# Revit family: bfs-15_240sug2_tug2_tua2_60Hz
name_source: partatom
category: 機械設備
units: mm (PartAtom-declared; Revit-internal decimal feet)

## family parameters
OmniClass タイトル = Centrifugal Fans
OmniClass 番号 = 23.75.35.17.27
パーツ タイプ = 割り込み
ロード時にボイドで切り取り = いいえ
丸型コネクタ寸法 = 直径を使用
作業面ベース = いいえ
共有 = いいえ
常に垂直 = はい
部屋計算ポイント = はい

## types (18) — shared parameters
Clearance Left = 450  [stored 1.47638 ft]
IfcExportAs = IfcFanType
IfcExportType = CENTRIFUGALFORWARDCURVED
MID静圧 = 0.0 Pa
MID風量 = 0.0 m³/h
OmniClassCode = 23-33 31 19 13 15
URL = https://www.mitsubishielectric.co.jp
Uniclass2015Code = Pr_65_67_29_12
Uniclass2015Title = Centrifugal fans
Uniclass2015Version = Systems v1.9
サービススペース = はい
ファンの種類 = 多翼形
仕様書バージョン = Version1.0
企業コード = 108420
分類コード = 50052502100020
参照している仕様書等のバージョン = 公共建築工事標準仕様書（機械設備工事編）平成31年度版
周波数 = 60 Hz
呼称 = 消音ボックス付送風機
実風量 = 0.0 m³/h
形名 = BFS-SUG : BFS-15SUG
本体マテリアル = 溶融亜鉛めっき鋼板
極 = 4
法定耐用年数 = 15
盤工事区分 = 電気工事
積算_科目 = 2 換気設備
製品リリース年月 = 2022年6月1日
製品出荷対象 = 国内
製造元 = 三菱電機株式会社
設置方法 = 天吊
説明 = ストレートシロッコファン天吊埋込タイプ（消音形）
負荷分類 = 3_ファン類
運転質量 = 0.00 kg
zero-valued in all types: Clearance Back, Clearance Bottom, Clearance Front, Clearance Right, Clearance Top

## per-type parameters (varying)
| type | Depth | Height | M | MAX静圧 | MAX風量 | MIN静圧 | MIN風量 | Width | ダクト径 | 価格 | 天吊金具ピッチ奥行 | 天吊金具ピッチ幅 | 極数 | 消費電力 | 番手 | 相 | 製品質量 | 質量 | 電動機出力 | 電圧 | 騒音レベル(dB(A)) | 騒音レベル(dB(A))_側面 | 騒音レベル(dB(A))_吐出 | 騒音レベル(dB(A))_吸込 |
| BFS-15SUG2 | 360  [stored 1.1811 ft] | 225  [stored 0.738189 ft] | 60  [stored 0.19685 ft] | 62.0 Pa | 150.0 m³/h | 25.0 Pa | 96.0 m³/h | 273  [stored 0.895669 ft] | 100 mm | 59900 $ | 325  [stored 1.06627 ft] | 349  [stored 1.14501 ft] | 2 | 24 W | #1 | 1 | 7.00 kg | 8.40 kg | 8 W | 100 V | 33 | 19 | 33 | 22 |
| BFS-30SUG2 | 428  [stored 1.4042 ft] | 225  [stored 0.738189 ft] | 70  [stored 0.229659 ft] | 39.0 Pa | 300.0 m³/h | 15.0 Pa | 182.0 m³/h | 273  [stored 0.895669 ft] | 150 mm | 83300 $ | 393  [stored 1.28937 ft] | 349  [stored 1.14501 ft] | 2 | 45 W | #1 | 1 | 7.50 kg | 9.00 kg | 16 W | 100 V | 40 | 19.5 | 40 | 26.5 |
| BFS-40SUG2 | 454  [stored 1.4895 ft] | 255  [stored 0.836614 ft] | 70  [stored 0.229659 ft] | 78.0 Pa | 400.0 m³/h | 37.0 Pa | 273.0 m³/h | 305  [stored 1.00066 ft] | 150 mm | 99500 $ | 419 | 381  [stored 1.25 ft] | 2 | 65 W | #1 1/4 | 1 | 9.50 kg | 11.40 kg | 25 W | 100 V | 44 | 20.5 | 44 | 27 |
| BFS-50SUG2 | 573  [stored 1.87992 ft] | 255  [stored 0.836614 ft] | 85  [stored 0.278871 ft] | 157.0 Pa | 500.0 m³/h | 81.0 Pa | 360.0 m³/h | 375  [stored 1.23031 ft] | 200 mm | 140000 $ | 538  [stored 1.76509 ft] | 451  [stored 1.47966 ft] | 2 | 88 W | #1 1/4 | 1 | 13.00 kg | 15.60 kg | 45 W | 100 V | 49 | 23 | 49 | 29.5 |
| BFS-65SUG2 | 638  [stored 2.09318 ft] | 305  [stored 1.00066 ft] | 85  [stored 0.278871 ft] | 157.0 Pa | 650.0 m³/h | 94.0 Pa | 501.0 m³/h | 423  [stored 1.3878 ft] | 200 mm | 148000 $ | 603 | 499  [stored 1.63714 ft] | 2 | 125 W | #1 1/4 | 1 | 16.00 kg | 19.20 kg | 65 W | 100 V | 51 | 24.5 | 51 | 29.5 |
| BFS-80SUG2 | 638  [stored 2.09318 ft] | 305  [stored 1.00066 ft] | 85  [stored 0.278871 ft] | 157.0 Pa | 800.0 m³/h | 84.0 Pa | 596.0 m³/h | 423  [stored 1.3878 ft] | 200 mm | 156000 $ | 603 | 499  [stored 1.63714 ft] | 2 | 159 W | #1 1/4 | 1 | 16.50 kg | 19.80 kg | 80 W | 100 V | 53 | 27 | 53 | 32 |
| BFS-90SUG2 | 638  [stored 2.09318 ft] | 305  [stored 1.00066 ft] | 85  [stored 0.278871 ft] | 206.0 Pa | 900.0 m³/h | 116.0 Pa | 676.0 m³/h | 443  [stored 1.45341 ft] | 200 mm | 164000 $ | 603 | 519 | 2 | 202 W | #1 1/2 | 1 | 18.50 kg | 22.20 kg | 110 W | 100 V | 55 | 29 | 55 | 34.5 |
| BFS-100SUG2 | 638  [stored 2.09318 ft] | 305  [stored 1.00066 ft] | 85  [stored 0.278871 ft] | 255.0 Pa | 1000.0 m³/h | 189.0 Pa | 861.0 m³/h | 443  [stored 1.45341 ft] | 200 mm | 176000 $ | 603 | 519 | 2 | 247 W | #1 1/2 | 1 | 19.00 kg | 22.80 kg | 160 W | 100 V | 58 | 31.5 | 58 | 37 |
| BFS-120SUG2 | 668 | 350  [stored 1.14829 ft] | 85  [stored 0.278871 ft] | 265.0 Pa | 1200.0 m³/h | 179.0 Pa | 989.0 m³/h | 455 | 250 mm | 194000 $ | 633  [stored 2.07677 ft] | 531  [stored 1.74213 ft] | 2 | 348 W | #1 1/2 | 1 | 22.00 kg | 26.40 kg | 200 W | 100 V | 58 | 32.5 | 58 | 41 |
| BFS-150SUG2 | 768 | 350  [stored 1.14829 ft] | 85  [stored 0.278871 ft] | 294.0 Pa | 1500.0 m³/h | 179.0 Pa | 1164.0 m³/h | 455 | 250 mm | 201000 $ | 733 | 531  [stored 1.74213 ft] | 2 | 484 W | #1 1/2 | 1 | 24.00 kg | 28.80 kg | 340 W | 100 V | 63 | 34 | 63 | 42.5 |
| BFS-80TUG2 | 638  [stored 2.09318 ft] | 305  [stored 1.00066 ft] | 85  [stored 0.278871 ft] | 157.0 Pa | 800.0 m³/h | 72.0 Pa | 542.0 m³/h | 423  [stored 1.3878 ft] | 200 mm | 156000 $ | 603 | 499  [stored 1.63714 ft] | 3 | 152 W | #1 1/4 | 3 | 18.00 kg | 21.60 kg | 80 W | 200 V | 53 | 26.5 | 53 | 32.5 |
| BFS-90TUG2 | 638  [stored 2.09318 ft] | 305  [stored 1.00066 ft] | 85  [stored 0.278871 ft] | 206.0 Pa | 900.0 m³/h | 95.0 Pa | 612.0 m³/h | 443  [stored 1.45341 ft] | 200 mm | 164000 $ | 603 | 519 | 3 | 187 W | #1 1/2 | 3 | 18.00 kg | 21.60 kg | 100 W | 200 V | 55 | 29 | 55 | 34.5 |
| BFS-100TUG2 | 638  [stored 2.09318 ft] | 305  [stored 1.00066 ft] | 85  [stored 0.278871 ft] | 255.0 Pa | 1000.0 m³/h | 124.0 Pa | 694.0 m³/h | 443  [stored 1.45341 ft] | 200 mm | 176000 $ | 603 | 519 | 3 | 230 W | #1 1/2 | 3 | 18.50 kg | 22.20 kg | 150 W | 200 V | 58 | 31 | 58 | 37 |
| BFS-120TUG2 | 668 | 350  [stored 1.14829 ft] | 85  [stored 0.278871 ft] | 265.0 Pa | 1200.0 m³/h | 119.0 Pa | 789.0 m³/h | 455 | 250 mm | 194000 $ | 633  [stored 2.07677 ft] | 531  [stored 1.74213 ft] | 3 | 319 W | #1 1/2 | 3 | 22.00 kg | 26.40 kg | 180 W | 200 V | 58 | 32.5 | 58 | 41 |
| BFS-150TUG2 | 768 | 350  [stored 1.14829 ft] | 85  [stored 0.278871 ft] | 294.0 Pa | 1500.0 m³/h | 142.0 Pa | 1046.0 m³/h | 455 | 250 mm | 201000 $ | 733 | 531  [stored 1.74213 ft] | 3 | 445 W | #1 1/2 | 3 | 24.00 kg | 28.80 kg | 280 W | 200 V | 63 | 34 | 63 | 42.5 |
| BFS-180TUG2 | 768 | 350  [stored 1.14829 ft] | 85  [stored 0.278871 ft] | 314.0 Pa | 1800.0 m³/h | 0.0 Pa | 0.0 m³/h | 505  [stored 1.65682 ft] | 250 mm | 236000 $ | 733 | 581  [stored 1.90617 ft] | 3 | 570 W | #1 1/2 | 3 | 26.00 kg | 31.20 kg | 350 W | 200 V | 64 | 34 | 64 | 43.5 |
| BFS-210TUG2 | 878 | 350  [stored 1.14829 ft] | 100  [stored 0.328084 ft] | 322.0 Pa | 2100.0 m³/h | 0.0 Pa | 0.0 m³/h | 551  [stored 1.80774 ft] | 300 mm | 310000 $ | 843 | 627  [stored 2.05709 ft] | 3 | 696 W | #1 1/2 | 3 | 29.00 kg | 34.80 kg | 490 W | 200 V | 67 | 34.5 | 67 | 45 |
| BFS-240TUA2 | 917 | 373  [stored 1.22375 ft] | 99  [stored 0.324803 ft] | 380.0 Pa | 2400.0 m³/h | 0.0 Pa | 0.0 m³/h | 493  [stored 1.61745 ft] | 300 mm | 304000 $ | 864 | 602  [stored 1.97507 ft] | 3 | 810 W | #1 1/2 | 3 | 37.00 kg | 44.40 kg | 1100 W | 200 V | 69 | 42 | 69 | 46.5 |

note: column(s) folded — value = type name in every type: モデル

note: [stored X ft] marks values corroborated as IEEE doubles in the binary element streams (Revit-internal decimal feet)
